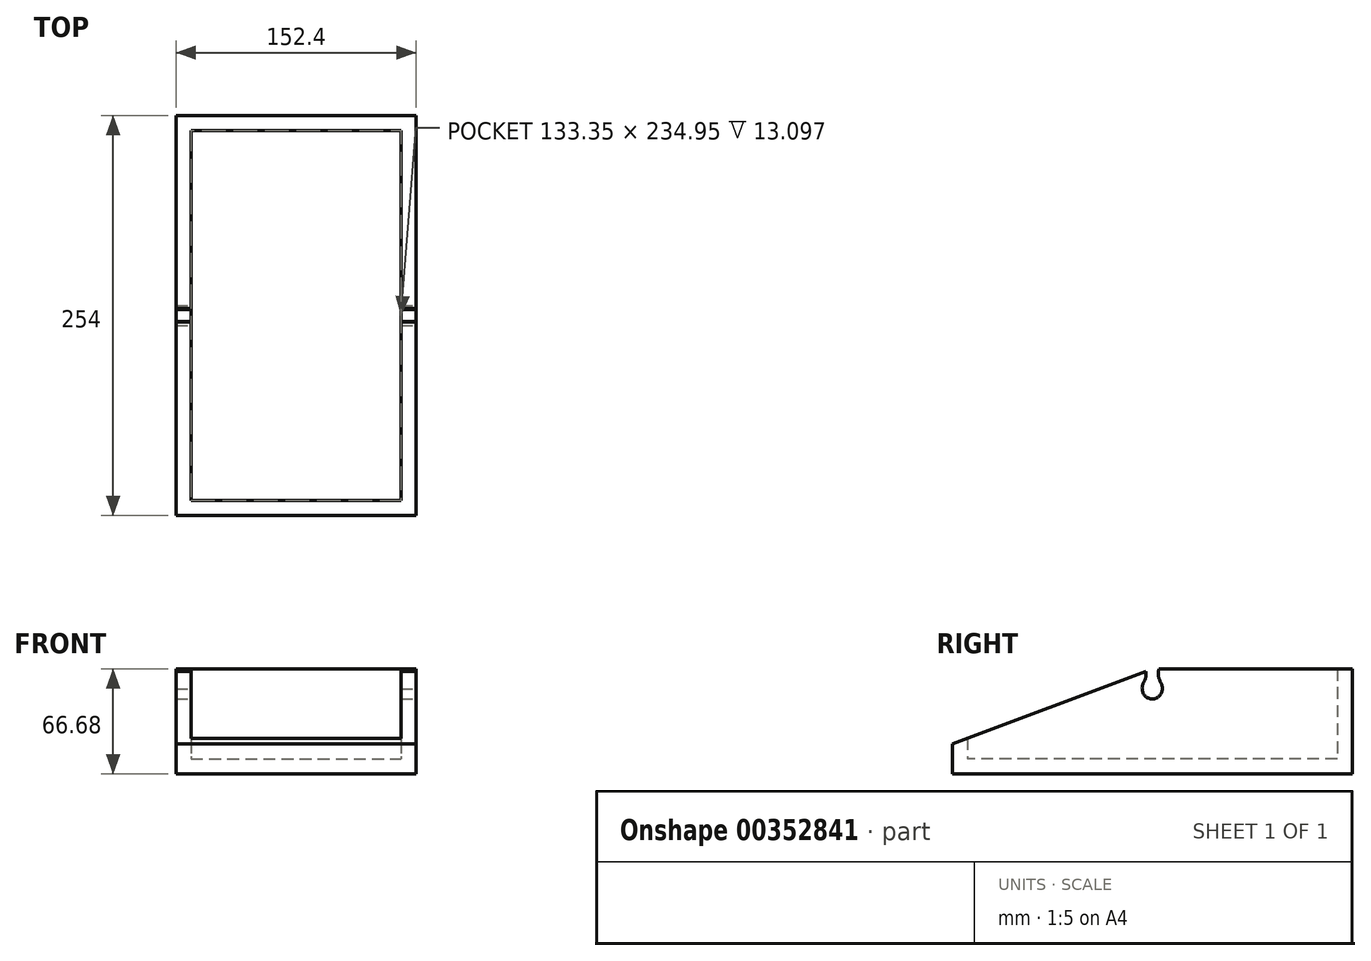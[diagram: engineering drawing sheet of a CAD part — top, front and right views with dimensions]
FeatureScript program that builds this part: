
annotation { "Feature Type Name" : "Feature", "Feature Type Description" : "" }
export const myFeature = defineFeature(function(context is Context, id is Id, definition is map)
    precondition{}
    {
        {
            var Q0;
            Q0=qCreatedBy(makeId("Top.planeOp"),FACE);
            var sketch = newSketch(context, id + "F0", { "sketchPlane" : qUnion([Q0])});
            skLineSegment(sketch, "E0.bottom", {"start": v(76.2, 127) * mm, "end": v(-76.2, 127) * mm});
            skLineSegment(sketch, "E0.top", {"start": v(76.2, -127) * mm, "end": v(-76.2, -127) * mm});
            skLineSegment(sketch, "E0.left", {"start": v(76.2, 127) * mm, "end": v(76.2, -127) * mm});
            skLineSegment(sketch, "E0.right", {"start": v(-76.2, 127) * mm, "end": v(-76.2, -127) * mm});
            skPoint(sketch, "E0.middle", {"position": v(0, 0) * mm});
            skSolve(sketch);
        }
        {
            var Q0;
            Q0 = qSketchRegion(id + "F0", true);
            extrude(context, id + "F1", {"entities" : qUnion([Q0]), "depth" : 9.52 * mm});
        }
        {
            var Q0;
            Q0=makeQuery(id+"F1.opExtrude","CAP_FACE",FACE,{"disambiguationData":[OSD([sQuery(id+"F0.wireOp",EDGE,"E0.bottom"),sQuery(id+"F0.wireOp",EDGE,"E0.top"),sQuery(id+"F0.wireOp",EDGE,"E0.left"),sQuery(id+"F0.wireOp",EDGE,"E0.right")])],"isStart":false});
            var sketch = newSketch(context, id + "F2", { "sketchPlane" : qUnion([Q0])});
            skLineSegment(sketch, "E1.bottom", {"start": v(-66.67, 117.48) * mm, "end": v(66.67, 117.48) * mm});
            skLineSegment(sketch, "E1.top", {"start": v(-66.67, -117.47) * mm, "end": v(66.67, -117.47) * mm});
            skLineSegment(sketch, "E1.left", {"start": v(-66.67, 117.47) * mm, "end": v(-66.67, -117.47) * mm});
            skLineSegment(sketch, "E1.right", {"start": v(66.67, 117.47) * mm, "end": v(66.67, -117.47) * mm});
            skPoint(sketch, "E1.middle", {"position": v(0, 0) * mm});
            skSolve(sketch);
        }
        {
            var Q0;
            Q0=makeQuery(id+"F2.imprint","IMPRINT",FACE,{"disambiguationData":[TD([[makeQuery(id+"F2.imprint","IMPRINT",EDGE,{"derivedFrom":sQuery(id+"F2.wireOp",EDGE,"E1.bottom")}),1.0]])]});
            extrude(context, id + "F3", {"entities" : qUnion([Q0]), "operationType" : NewBodyOperationType.ADD, "depth" : 57.15 * mm});
        }
        {
            var Q0;
            {var subQ0=sQuery(id+"F0.wireOp",EDGE,"E0.left");Q0=makeQuery(id+"F3.boolean.opBoolean","MERGE",FACE,{"derivedFrom":[makeQuery(id+"F1.opExtrude","SWEPT_FACE",FACE,{"disambiguationData":[OSD([subQ0])]}),makeQuery(id+"F3.opExtrude","SWEPT_FACE",FACE,{"disambiguationData":[OSD([subQ0])]})]});}
            var sketch = newSketch(context, id + "F4", { "sketchPlane" : qUnion([Q0])});
            skLineSegment(sketch, "E2", {"start": v(-127, 19.05) * mm, "end": v(0, 66.68) * mm});
            skLineSegment(sketch, "E3", {"start": v(0, 66.68) * mm, "end": v(-127, 66.68) * mm});
            skLineSegment(sketch, "E4", {"start": v(-127, 66.68) * mm, "end": v(-127, 19.05) * mm});
            skCircle(sketch, "E5", {"center": v(0, 53.98) * mm, "radius": 6.35 * mm});
            skFitSpline(sketch, "E6", {"points": [v(6.35, 53.98) * mm, v(5.15, 58.63) * mm, v(4.07, 61.48) * mm, v(4.3, 66.68) * mm], "startDerivative": vector(2.17, 15.68) * mm, "endDerivative": vector(3.87, 16.2) * mm});
            skFitSpline(sketch, "E7.MirrorCS", {"points": [v(-6.35, 53.98) * mm, v(-5.15, 58.63) * mm, v(-4.07, 61.48) * mm, v(-4.3, 66.68) * mm], "startDerivative": vector(-2.17, 15.68) * mm, "endDerivative": vector(-3.87, 16.2) * mm});
            skSolve(sketch);
        }
        {
            var Q0;
            {var subQ0=sQuery(id+"F4.wireOp",EDGE,"E4");Q0=makeQuery(id+"F4.imprint","IMPRINT",FACE,{"disambiguationData":[TD([[makeQuery(id+"F4.imprint","IMPRINT",EDGE,{"derivedFrom":subQ0}),1.0]])]});}
            var Q1;
            {var subQ5=sQuery(id+"F4.wireOp",EDGE,"E6");Q1=makeQuery(id+"F4.imprint","IMPRINT",FACE,{"disambiguationData":[TD([[makeQuery(id+"F4.imprint","IMPRINT",EDGE,{"derivedFrom":subQ5}),1.0]])]});}
            var Q2;
            {var subQ0=sQuery(id+"F4.wireOp",EDGE,"E5");var subQ1=makeQuery(id+"F4.imprint","INTERSECT",VERTEX,{"derivedFrom":[subQ0,sQuery(id+"F4.wireOp",EDGE,"E6")]});Q2=makeQuery(id+"F4.imprint","IMPRINT",FACE,{"disambiguationData":[TD([[makeQuery(id+"F4.imprint","IMPRINT",EDGE,{"disambiguationData":[TD([[subQ1,-1.0]])],"derivedFrom":subQ0}),1.0]])]});}
            var Q3;
            {var subQ0=sQuery(id+"F4.wireOp",EDGE,"E3");var subQ3=sQuery(id+"F4.wireOp",EDGE,"E7.MirrorCS");var subQ5=makeQuery(id+"F4.imprint","INTERSECT",VERTEX,{"derivedFrom":[subQ0,subQ3]});Q3=makeQuery(id+"F4.imprint","IMPRINT",FACE,{"disambiguationData":[TD([[makeQuery(id+"F4.imprint","IMPRINT",EDGE,{"disambiguationData":[TD([[subQ5,1.0]])],"derivedFrom":subQ3}),-1.0]])]});}
            extrude(context, id + "F5", {"entities" : qUnion([Q0, Q1, Q2, Q3]), "operationType" : NewBodyOperationType.REMOVE, "endBound" : BoundingType.THROUGH_ALL, "oppositeDirection" : true, "depth" : 25.4 * mm});
        }
    });
